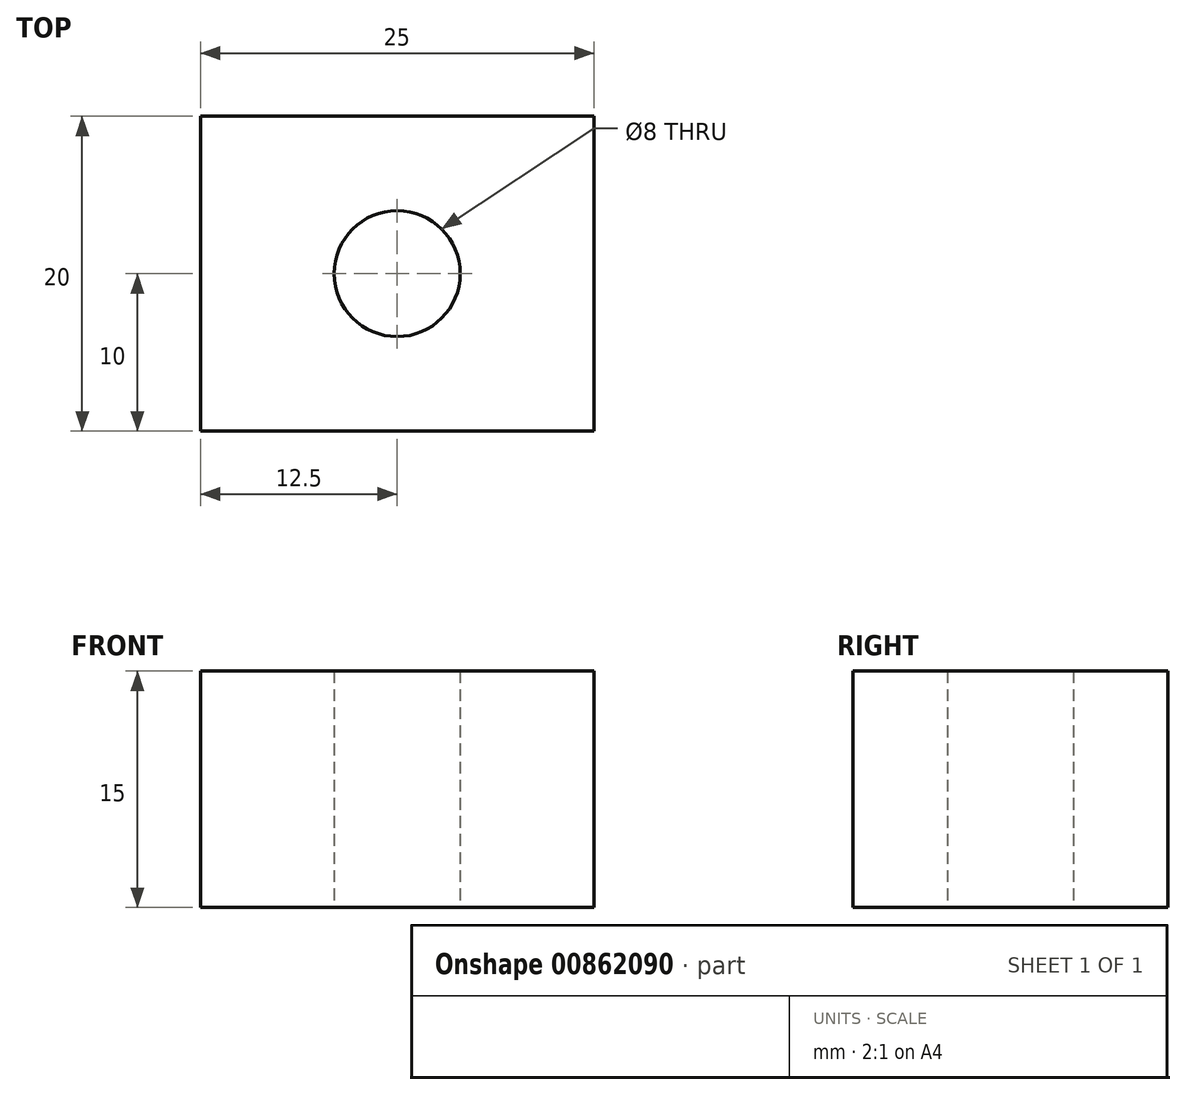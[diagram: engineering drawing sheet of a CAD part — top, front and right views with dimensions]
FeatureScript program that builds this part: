
annotation { "Feature Type Name" : "Feature", "Feature Type Description" : "" }
export const myFeature = defineFeature(function(context is Context, id is Id, definition is map)
    precondition{}
    {
        {
            var Q0;
            Q0=qCreatedBy(makeId("Top.planeOp"),FACE);
            var sketch = newSketch(context, id + "F0", { "sketchPlane" : qUnion([Q0])});
            skLineSegment(sketch, "E0.bottom", {"start": v(0, 0) * mm, "end": v(25, 0) * mm});
            skLineSegment(sketch, "E0.top", {"start": v(0, -20) * mm, "end": v(25, -20) * mm});
            skLineSegment(sketch, "E0.left", {"start": v(0, 0) * mm, "end": v(0, -20) * mm});
            skLineSegment(sketch, "E0.right", {"start": v(25, 0) * mm, "end": v(25, -20) * mm});
            skLineSegment(sketch, "E1", {"start": v(0, -10) * mm, "end": v(25, -10) * mm, "construction": true});
            skCircle(sketch, "E2", {"center": v(12.5, -10) * mm, "radius": 4 * mm});
            skSolve(sketch);
        }
        {
            var Q0;
            Q0=makeQuery(id+"F0.imprint","IMPRINT",FACE,{"disambiguationData":[TD([[makeQuery(id+"F0.imprint","IMPRINT",EDGE,{"derivedFrom":sQuery(id+"F0.wireOp",EDGE,"E0.bottom")}),-1.0]])]});
            extrude(context, id + "F1", {"entities" : qUnion([Q0]), "depth" : 15 * mm, "offsetDistance" : 25.4 * mm});
        }
    });
